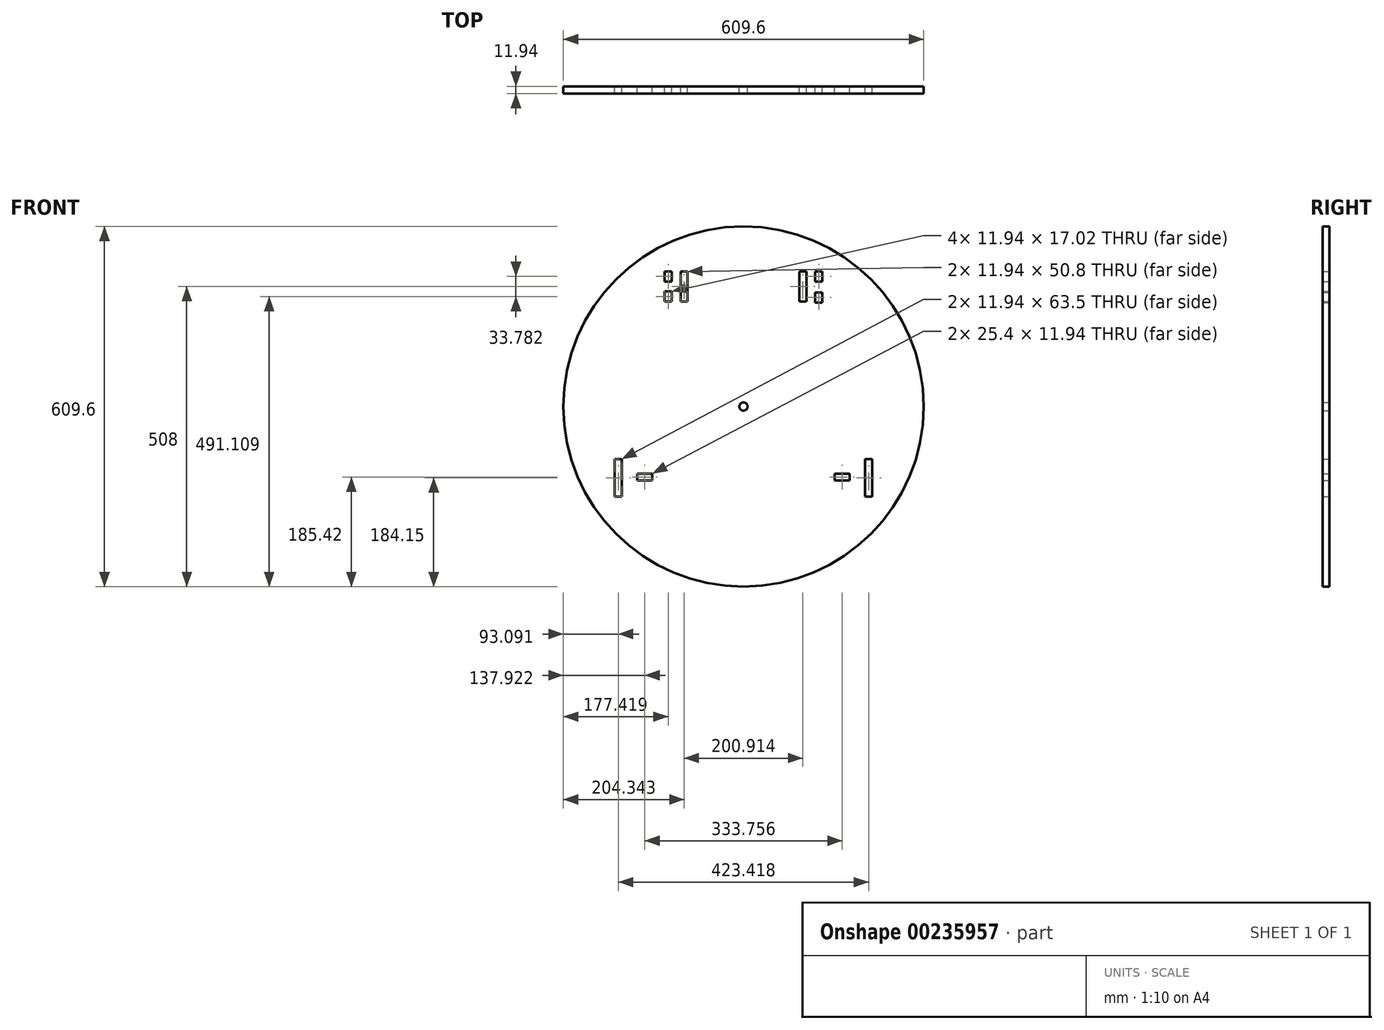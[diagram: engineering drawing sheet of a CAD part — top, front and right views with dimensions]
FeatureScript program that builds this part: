
annotation { "Feature Type Name" : "Feature", "Feature Type Description" : "" }
export const myFeature = defineFeature(function(context is Context, id is Id, definition is map)
    precondition{}
    {
        {
            var Q0;
            Q0=qCreatedBy(makeId("Front.planeOp"),FACE);
            var sketch = newSketch(context, id + "F0", { "sketchPlane" : qUnion([Q0])});
            skCircle(sketch, "E0", {"center": v(0, 0) * mm, "radius": 304.8 * mm});
            skCircle(sketch, "E1", {"center": v(0, 0) * mm, "radius": 6.99 * mm});
            skLineSegment(sketch, "E2", {"start": v(-263.96, 152.4) * mm, "end": v(263.96, 152.4) * mm});
            skLineSegment(sketch, "E3", {"start": v(0, 152.4) * mm, "end": v(0, 304.8) * mm});
            skLineSegment(sketch, "E4", {"start": v(0, 228.6) * mm, "end": v(94.49, 228.6) * mm});
            skLineSegment(sketch, "E5", {"start": v(0, 228.6) * mm, "end": v(-94.49, 228.6) * mm});
            skLineSegment(sketch, "E6", {"start": v(-94.49, 228.6) * mm, "end": v(-94.49, 177.8) * mm});
            skLineSegment(sketch, "E7", {"start": v(94.49, 228.6) * mm, "end": v(94.49, 177.8) * mm});
            skLineSegment(sketch, "E8", {"start": v(-94.49, 177.8) * mm, "end": v(-106.43, 177.8) * mm});
            skLineSegment(sketch, "E9", {"start": v(-94.49, 228.6) * mm, "end": v(-106.43, 228.6) * mm});
            skLineSegment(sketch, "E10", {"start": v(94.49, 177.8) * mm, "end": v(106.43, 177.8) * mm});
            skLineSegment(sketch, "E11", {"start": v(-106.43, 228.6) * mm, "end": v(-106.43, 177.8) * mm});
            skLineSegment(sketch, "E12", {"start": v(94.49, 228.6) * mm, "end": v(106.43, 228.6) * mm});
            skLineSegment(sketch, "E13", {"start": v(106.43, 228.6) * mm, "end": v(106.43, 177.8) * mm});
            skLineSegment(sketch, "E14", {"start": v(0, 0) * mm, "end": v(0, -152.4) * mm});
            skLineSegment(sketch, "E15", {"start": v(0, -152.4) * mm, "end": v(-205.74, -152.4) * mm});
            skLineSegment(sketch, "E16", {"start": v(0, -152.4) * mm, "end": v(205.74, -152.4) * mm});
            skLineSegment(sketch, "E17", {"start": v(-205.74, -152.4) * mm, "end": v(-205.74, -88.9) * mm});
            skLineSegment(sketch, "E18", {"start": v(205.74, -152.4) * mm, "end": v(205.74, -88.9) * mm});
            skLineSegment(sketch, "E19", {"start": v(-205.74, -152.4) * mm, "end": v(-217.68, -152.4) * mm});
            skLineSegment(sketch, "E20", {"start": v(205.74, -152.4) * mm, "end": v(217.68, -152.4) * mm});
            skLineSegment(sketch, "E21", {"start": v(-217.68, -152.4) * mm, "end": v(-217.68, -88.9) * mm});
            skLineSegment(sketch, "E22", {"start": v(217.68, -152.4) * mm, "end": v(217.68, -88.9) * mm});
            skLineSegment(sketch, "E23", {"start": v(-217.68, -88.9) * mm, "end": v(-205.74, -88.9) * mm});
            skLineSegment(sketch, "E24", {"start": v(205.74, -88.9) * mm, "end": v(217.68, -88.9) * mm});
            skPoint(sketch, "E25.endSnap0", {"position": v(-205.74, -120.65) * mm});
            skPoint(sketch, "E26.endSnap0", {"position": v(205.74, -120.65) * mm});
            skPoint(sketch, "E27.endSnap0", {"position": v(217.68, -120.65) * mm});
            skLineSegment(sketch, "E28", {"start": v(0, 228.6) * mm, "end": v(133.35, 228.6) * mm});
            skLineSegment(sketch, "E29.bottom", {"start": v(133.35, 228.6) * mm, "end": v(121.41, 228.6) * mm});
            skLineSegment(sketch, "E29.top", {"start": v(133.35, 211.58) * mm, "end": v(121.41, 211.58) * mm});
            skLineSegment(sketch, "E29.left", {"start": v(133.35, 228.6) * mm, "end": v(133.35, 211.58) * mm});
            skLineSegment(sketch, "E29.right", {"start": v(121.41, 228.6) * mm, "end": v(121.41, 211.58) * mm});
            skLineSegment(sketch, "E30.bottom", {"start": v(133.35, 176.17) * mm, "end": v(121.41, 176.17) * mm});
            skLineSegment(sketch, "E30.top", {"start": v(133.35, 193.18) * mm, "end": v(121.41, 193.18) * mm});
            skLineSegment(sketch, "E30.left", {"start": v(133.35, 176.17) * mm, "end": v(133.35, 193.18) * mm});
            skLineSegment(sketch, "E30.right", {"start": v(121.41, 176.17) * mm, "end": v(121.41, 193.18) * mm});
            skLineSegment(sketch, "E31", {"start": v(0, 228.6) * mm, "end": v(-133.35, 228.6) * mm});
            skLineSegment(sketch, "E32.bottom", {"start": v(-133.35, 228.6) * mm, "end": v(-121.41, 228.6) * mm});
            skLineSegment(sketch, "E32.top", {"start": v(-133.35, 211.58) * mm, "end": v(-121.41, 211.58) * mm});
            skLineSegment(sketch, "E32.left", {"start": v(-133.35, 228.6) * mm, "end": v(-133.35, 211.58) * mm});
            skLineSegment(sketch, "E32.right", {"start": v(-121.41, 228.6) * mm, "end": v(-121.41, 211.58) * mm});
            skLineSegment(sketch, "E33.bottom", {"start": v(-133.35, 177.8) * mm, "end": v(-121.41, 177.8) * mm});
            skLineSegment(sketch, "E33.top", {"start": v(-133.35, 194.82) * mm, "end": v(-121.41, 194.82) * mm});
            skLineSegment(sketch, "E33.left", {"start": v(-133.35, 177.8) * mm, "end": v(-133.35, 194.82) * mm});
            skLineSegment(sketch, "E33.right", {"start": v(-121.41, 177.8) * mm, "end": v(-121.41, 194.82) * mm});
            skLineSegment(sketch, "E34", {"start": v(-179.58, -113.41) * mm, "end": v(-179.58, -125.35) * mm});
            skLineSegment(sketch, "E35", {"start": v(-179.58, -113.41) * mm, "end": v(-154.18, -113.41) * mm});
            skLineSegment(sketch, "E36", {"start": v(-179.58, -125.35) * mm, "end": v(-154.18, -125.35) * mm});
            skLineSegment(sketch, "E37", {"start": v(-154.18, -113.41) * mm, "end": v(-154.18, -125.35) * mm});
            skLineSegment(sketch, "E38", {"start": v(179.58, -113.41) * mm, "end": v(179.58, -125.35) * mm});
            skLineSegment(sketch, "E39", {"start": v(179.58, -113.41) * mm, "end": v(154.18, -113.41) * mm});
            skLineSegment(sketch, "E40", {"start": v(179.58, -125.35) * mm, "end": v(154.18, -125.35) * mm});
            skLineSegment(sketch, "E41", {"start": v(154.18, -113.41) * mm, "end": v(154.18, -125.35) * mm});
            skSolve(sketch);
        }
        {
            var Q0;
            Q0=makeQuery(id+"F0.imprint","IMPRINT",FACE,{"disambiguationData":[TD([[makeQuery(id+"F0.imprint","IMPRINT",EDGE,{"derivedFrom":sQuery(id+"F0.wireOp",EDGE,"E0")}),1.0]])]});
            var Q1;
            Q1=makeQuery(id+"F0.imprint","IMPRINT",FACE,{"disambiguationData":[TD([[makeQuery(id+"F0.imprint","IMPRINT",EDGE,{"derivedFrom":sQuery(id+"F0.wireOp",EDGE,"E1")}),-1.0]])]});
            extrude(context, id + "F1", {"entities" : qUnion([Q0, Q1]), "depth" : 11.94 * mm});
        }
    });
